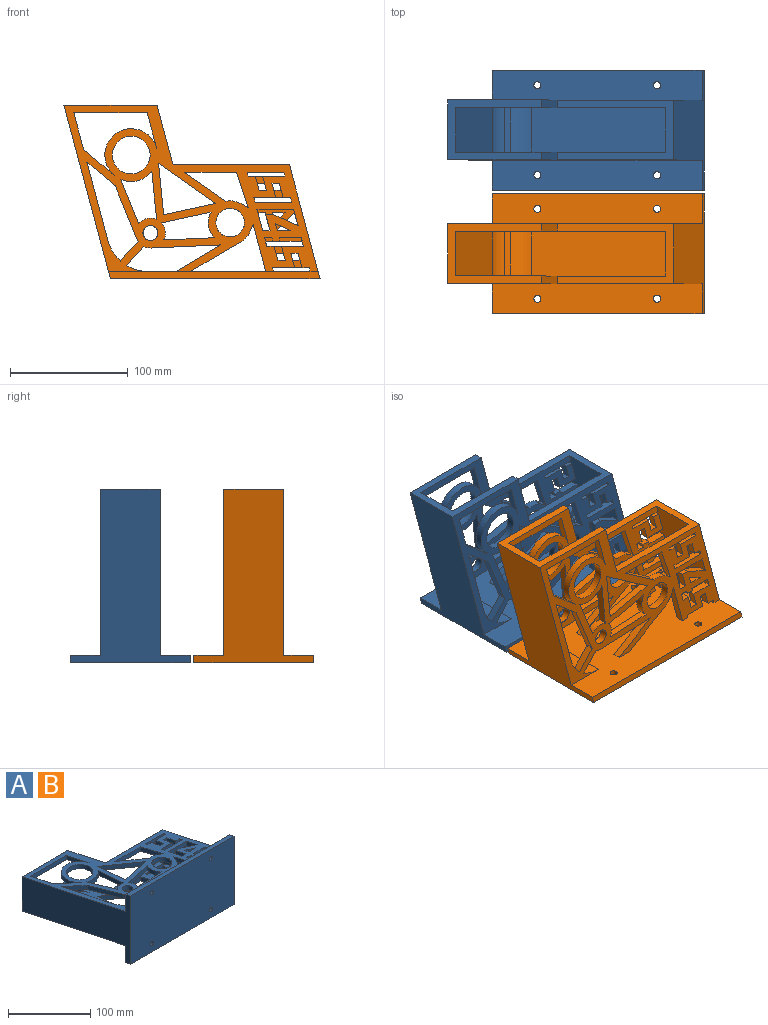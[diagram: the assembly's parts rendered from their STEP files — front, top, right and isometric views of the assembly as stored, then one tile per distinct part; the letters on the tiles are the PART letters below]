
ASSEMBLY  parts=2 mates=1
PART A: 172 faces, bbox 217.1x147.2x101.6 mm
  f0: plane 16.15x14.78mm, normal (0.74,-0.68,0), area 139mm2, adj f15,f17,f53,f170
  f1: plane 177.63x101.6mm, normal (0,1,0), area 15687.5mm2, adj f2,f6,f10,f15,f16,f17,f19,f22
  f2: plane 215.38x140.86mm, normal (0,0,1), area 9095.8mm2, adj f1,f3,f11,f12,f13,f14,f18,f19
  f3: cylinder r=18.51mm len=8.94mm, axis (0,0,1), area 76.2mm2, adj f2,f16,f84,f162
  f4: cylinder r=18.51mm len=13.03mm, axis (0,0,-1), area 85.7mm2, adj f15,f17,f153,f160
  f5: plane 30.14x9.86mm, normal (-0.95,-0.31,0), area 201.3mm2, adj f15,f17,f154,f160
  f6: plane 40.06x10.73mm, normal (-0.97,-0.26,0), area 263.3mm2, adj f1,f15,f17,f159
  f7: plane 7.17x6.35mm, normal (0.97,0.26,0), area 47.1mm2, adj f15,f17,f135,f152
  f8: plane 18.05x6.35mm, normal (0.97,0.26,0), area 118.7mm2, adj f15,f17,f130,f134
  f9: plane 6.35x4.2mm, normal (0.97,0.26,0), area 27.6mm2, adj f15,f17,f125,f129
  f10: plane 6.35x3.18mm, normal (0.97,0.26,0), area 20.9mm2, adj f1,f15,f17,f124
  f11: plane 7.21x6.35mm, normal (0.97,0.26,0), area 47.4mm2, adj f2,f16,f100,f109
  f12: plane 18.01x6.35mm, normal (0.97,0.26,0), area 118.4mm2, adj f2,f16,f96,f99
  f13: plane 6.35x4.2mm, normal (0.97,0.26,0), area 27.6mm2, adj f2,f16,f86,f95
  f14: plane 6.35x3.18mm, normal (0.97,0.26,0), area 20.9mm2, adj f2,f16,f82,f85
  f15: plane 201.38x140.86mm, normal (0,0,1), area 7397.1mm2, adj f0,f1,f4,f5,f6,f7,f8,f9
  f16: plane 201.38x140.86mm, normal (0,0,-1), area 7441.4mm2, adj f1,f3,f11,f12,f13,f14,f18,f20
  f17: plane 215.38x140.86mm, normal (0,0,-1), area 9051.5mm2, adj f0,f1,f4,f5,f6,f7,f8,f9
  f18: plane 115.46x50.8mm, normal (0.97,0.26,0), area 5847.6mm2, adj f2,f15,f16,f17,f20,f33,f34,f55
  f19: plane 101.6x96.58mm, normal (0.97,0.26,0), area 5413.5mm2, adj f1,f2,f17,f23,f25,f163,f164
  f20: plane 78.89x50.8mm, normal (0,1,0), area 1252.3mm2, adj f2,f15,f16,f17,f18,f21,f22,f28
  f21: plane 50.62x13.56mm, normal (0.97,0.26,0), area 332.8mm2, adj f2,f16,f20,f25
  f22: plane 147.21x101.6mm, normal (-0.97,-0.26,0), area 8075.9mm2, adj f1,f2,f17,f20,f23,f163,f164
  f23: plane 177.63x101.6mm, normal (0,-1,0), area 17932.8mm2, adj f19,f22,f163,f164,f165,f166,f167,f168
  f24: cylinder r=16mm len=32mm, axis (0,0,1), area 638.5mm2, adj f2,f16
  f25: plane 98.75x50.8mm, normal (0,1,0), area 1504.5mm2, adj f2,f15,f16,f17,f19,f21,f28,f32
  f26: cylinder r=6.35mm len=12.7mm, axis (0,0,1), area 253.4mm2, adj f2,f16
  f27: cylinder r=12.16mm len=24.32mm, axis (0,0,1), area 485.1mm2, adj f2,f16
  f28: plane 50.62x13.56mm, normal (0.97,0.26,0), area 332.8mm2, adj f15,f17,f20,f25
  f29: cylinder r=6.35mm len=12.7mm, axis (0,0,-1), area 253.4mm2, adj f15,f17
  f30: cylinder r=12.16mm len=24.32mm, axis (0,0,-1), area 485.1mm2, adj f15,f17
  f31: cylinder r=16mm len=32mm, axis (0,0,1), area 638.5mm2, adj f15,f17
  f32: plane 90.23x50.8mm, normal (-0.97,-0.26,0), area 4002.5mm2, adj f1,f2,f15,f16,f17,f25,f62,f82
  f33: plane 26x21.92mm, normal (0.64,0.76,0), area 215.9mm2, adj f15,f17,f18,f36
  f34: plane 62.26x6.35mm, normal (0,-1,0), area 395.3mm2, adj f15,f17,f18,f35
  f35: plane 30.18x8.09mm, normal (-0.97,-0.26,0), area 198.4mm2, adj f15,f17,f34,f36
  f36: cylinder r=22.35mm len=43.94mm, axis (0,0,1), area 532.3mm2, adj f15,f17,f33,f35
  f37: plane 48.53x34.15mm, normal (-0.58,-0.82,0), area 376.8mm2, adj f15,f17,f38,f39
  f38: plane 44.16x9.65mm, normal (-0.21,0.98,0), area 287mm2, adj f15,f17,f37,f39
  f39: plane 43.8x6.35mm, normal (1,0.1,0), area 279.5mm2, adj f15,f17,f37,f38
  f40: plane 40.57x6.35mm, normal (-1,-0.1,0), area 258.9mm2, adj f15,f17,f41,f43
  f41: cylinder r=12.7mm len=15.24mm, axis (0,0,1), area 107.4mm2, adj f15,f17,f40,f42
  f42: plane 37.8x15.27mm, normal (0.93,0.37,0), area 258.9mm2, adj f15,f17,f41,f43
  f43: cylinder r=22.35mm len=26.46mm, axis (0,0,1), area 186.1mm2, adj f15,f17,f40,f42
  f44: cylinder r=18.51mm len=21.66mm, axis (0,0,1), area 148.4mm2, adj f15,f17,f45,f47
  f45: plane 42.89x6.35mm, normal (-0.04,1,0), area 272.6mm2, adj f15,f17,f44,f46
  f46: cylinder r=12.7mm len=14.41mm, axis (0,0,1), area 98.2mm2, adj f15,f17,f45,f47
  f47: plane 41.94x9.16mm, normal (0.21,-0.98,0), area 272.6mm2, adj f15,f17,f44,f46
  f48: plane 16.15x14.78mm, normal (0.74,-0.68,0), area 139mm2, adj f2,f16,f54,f170
  f49: plane 37.73x22.39mm, normal (-0.51,0.86,0), area 278.6mm2, adj f1,f15,f17,f51
  f50: plane 37.73x22.39mm, normal (-0.51,0.86,0), area 278.6mm2, adj f1,f2,f16,f52
  f51: plane 59.01x6.35mm, normal (0.04,-1,0), area 375.1mm2, adj f15,f17,f49,f53
  f52: plane 59.01x6.35mm, normal (0.04,-1,0), area 375.1mm2, adj f2,f16,f50,f54
  f53: cylinder r=12.7mm len=6.35mm, axis (0,0,1), area 41mm2, adj f0,f15,f17,f51
  f54: cylinder r=12.7mm len=6.35mm, axis (0,0,1), area 41mm2, adj f2,f16,f48,f52
  f55: plane 23.98x20.21mm, normal (-0.64,-0.76,0), area 199.1mm2, adj f15,f17,f18,f60
  f56: plane 23.98x20.21mm, normal (-0.64,-0.76,0), area 199.1mm2, adj f2,f16,f18,f61
  f57: plane 50.8x16.52mm, normal (-0.74,0.68,0), area 309.5mm2, adj f2,f15,f16,f17,f58,f59,f169,f171
  f58: cylinder r=12.7mm len=6.35mm, axis (0,0,1), area 17.6mm2, adj f15,f17,f57,f60
  f59: cylinder r=12.7mm len=6.35mm, axis (0,0,1), area 17.6mm2, adj f2,f16,f57,f61
  f60: plane 44.73x18.07mm, normal (-0.93,-0.37,0), area 306.3mm2, adj f15,f17,f55,f58
  f61: plane 44.73x18.07mm, normal (-0.93,-0.37,0), area 306.3mm2, adj f2,f16,f56,f59
  f62: plane 31.13x6.35mm, normal (0,-1,0), area 197.7mm2, adj f15,f17,f32,f63
  f63: plane 6.35x3.18mm, normal (0.97,0.26,0), area 20.9mm2, adj f15,f17,f62,f143
  f64: plane 42.73x25.36mm, normal (0.51,-0.86,0), area 315.5mm2, adj f1,f15,f17,f65
  f65: cylinder r=18.51mm len=8.94mm, axis (0,0,1), area 76.2mm2, adj f15,f17,f64,f159
  f66: cylinder r=22.35mm len=43.94mm, axis (0,0,1), area 532.3mm2, adj f2,f16,f67,f69
  f67: plane 30.18x8.09mm, normal (-0.97,-0.26,0), area 198.4mm2, adj f2,f16,f66,f68
  f68: plane 62.26x6.35mm, normal (0,-1,0), area 395.3mm2, adj f2,f16,f18,f67
  f69: plane 26x21.92mm, normal (0.64,0.76,0), area 215.9mm2, adj f2,f16,f18,f66
  f70: plane 43.8x6.35mm, normal (1,0.1,0), area 279.5mm2, adj f2,f16,f71,f72
  f71: plane 44.16x9.65mm, normal (-0.21,0.98,0), area 287mm2, adj f2,f16,f70,f72
  f72: plane 48.53x34.15mm, normal (-0.58,-0.82,0), area 376.8mm2, adj f2,f16,f70,f71
  f73: cylinder r=22.35mm len=26.46mm, axis (0,0,1), area 186.1mm2, adj f2,f16,f74,f76
  f74: plane 37.8x15.27mm, normal (0.93,0.37,0), area 258.9mm2, adj f2,f16,f73,f75
  f75: cylinder r=12.7mm len=15.24mm, axis (0,0,1), area 107.4mm2, adj f2,f16,f74,f76
  f76: plane 40.57x6.35mm, normal (-1,-0.1,0), area 258.9mm2, adj f2,f16,f73,f75
  f77: plane 41.94x9.16mm, normal (0.21,-0.98,0), area 272.6mm2, adj f2,f16,f78,f80
  f78: cylinder r=12.7mm len=14.41mm, axis (0,0,1), area 98.2mm2, adj f2,f16,f77,f79
  f79: plane 42.89x6.35mm, normal (-0.04,1,0), area 272.6mm2, adj f2,f16,f78,f80
  f80: cylinder r=18.51mm len=21.66mm, axis (0,0,1), area 148.4mm2, adj f2,f16,f77,f79
  f81: plane 6.35x3.18mm, normal (0.97,0.26,0), area 20.9mm2, adj f1,f2,f16,f110
  f82: plane 31.13x6.35mm, normal (0,-1,0), area 197.7mm2, adj f2,f14,f16,f32
  f83: plane 40.06x10.73mm, normal (-0.97,-0.26,0), area 263.3mm2, adj f1,f2,f16,f162
  f84: plane 42.73x25.36mm, normal (0.51,-0.86,0), area 315.5mm2, adj f1,f2,f3,f16
  f85: plane 6.35x6.23mm, normal (0,1,0), area 39.5mm2, adj f2,f14,f16,f94
  f86: plane 18.68x6.35mm, normal (0,-1,0), area 118.6mm2, adj f2,f13,f16,f87
  f87: plane 12.03x6.35mm, normal (0.97,0.26,0), area 79.1mm2, adj f2,f16,f86,f88
  f88: plane 6.35x6.23mm, normal (0,-1,0), area 39.5mm2, adj f2,f16,f87,f89
  f89: plane 12.03x6.35mm, normal (-0.97,-0.26,0), area 79.1mm2, adj f2,f16,f88,f90
  f90: plane 6.35x6.23mm, normal (0,-1,0), area 39.5mm2, adj f2,f16,f32,f89
  f91: plane 18.68x6.35mm, normal (0,1,0), area 118.6mm2, adj f2,f16,f32,f92
  f92: plane 12.03x6.35mm, normal (-0.97,-0.26,0), area 79.1mm2, adj f2,f16,f91,f93
  f93: plane 6.35x6.23mm, normal (0,1,0), area 39.5mm2, adj f2,f16,f92,f94
  f94: plane 12.03x6.35mm, normal (0.97,0.26,0), area 79.1mm2, adj f2,f16,f85,f93
  f95: plane 31.13x6.35mm, normal (0,1,0), area 197.7mm2, adj f2,f13,f16,f32
  f96: plane 31.13x6.35mm, normal (0,-1,0), area 197.7mm2, adj f2,f12,f16,f32
  f97: plane 11.57x6.35mm, normal (0,1,0), area 73.4mm2, adj f2,f16,f98,f108
  f98: plane 6.35x6.01mm, normal (0.97,0.26,0), area 39.5mm2, adj f2,f16,f97,f108
  f99: plane 6.35x6.23mm, normal (0,1,0), area 39.5mm2, adj f2,f12,f16,f107
  f100: plane 6.35x6.23mm, normal (0,-1,0), area 39.5mm2, adj f2,f11,f16,f101
  f101: plane 6.35x3.01mm, normal (-0.97,-0.26,0), area 19.8mm2, adj f2,f16,f100,f102
  f102: plane 6.35x6.23mm, normal (0,-1,0), area 39.5mm2, adj f2,f16,f101,f103
  f103: plane 6.35x3.01mm, normal (0.97,0.26,0), area 19.8mm2, adj f2,f16,f102,f104
  f104: plane 18.68x6.35mm, normal (0,-1,0), area 118.6mm2, adj f2,f16,f32,f103
  f105: plane 21.28x9.71mm, normal (0.42,0.91,0), area 148.5mm2, adj f2,f16,f32,f106
  f106: plane 6.35x6.23mm, normal (0,1,0), area 39.5mm2, adj f2,f16,f105,f107
  f107: plane 13.81x6.35mm, normal (-0.97,-0.26,0), area 90.8mm2, adj f2,f16,f99,f106
  f108: plane 13.18x6.35mm, normal (-0.42,-0.91,0), area 92mm2, adj f2,f16,f97,f98
  f109: plane 6.35x6.23mm, normal (0,1,0), area 39.5mm2, adj f2,f11,f16,f118
  f110: plane 18.68x6.35mm, normal (0,-1,0), area 118.6mm2, adj f2,f16,f81,f111
  f111: plane 12.03x6.35mm, normal (0.97,0.26,0), area 79.1mm2, adj f2,f16,f110,f112
  f112: plane 6.35x6.23mm, normal (0,-1,0), area 39.5mm2, adj f2,f16,f111,f113
  f113: plane 12.03x6.35mm, normal (-0.97,-0.26,0), area 79.1mm2, adj f2,f16,f112,f114
  f114: plane 6.35x6.23mm, normal (0,-1,0), area 39.5mm2, adj f2,f16,f32,f113
  f115: plane 18.68x6.35mm, normal (0,1,0), area 118.6mm2, adj f2,f16,f32,f116
  f116: plane 12.03x6.35mm, normal (-0.97,-0.26,0), area 79.1mm2, adj f2,f16,f115,f117
  f117: plane 6.35x6.23mm, normal (0,1,0), area 39.5mm2, adj f2,f16,f116,f118
  f118: plane 12.03x6.35mm, normal (0.97,0.26,0), area 79.1mm2, adj f2,f16,f109,f117
  f119: plane 6.35x6.23mm, normal (0,1,0), area 39.5mm2, adj f15,f17,f32,f128
  f120: plane 18.68x6.35mm, normal (0,-1,0), area 118.6mm2, adj f15,f17,f32,f121
  f121: plane 12.03x6.35mm, normal (-0.97,-0.26,0), area 79.1mm2, adj f15,f17,f120,f122
  f122: plane 6.35x6.23mm, normal (0,-1,0), area 39.5mm2, adj f15,f17,f121,f123
  f123: plane 12.03x6.35mm, normal (0.97,0.26,0), area 79.1mm2, adj f15,f17,f122,f124
  f124: plane 6.35x6.23mm, normal (0,-1,0), area 39.5mm2, adj f10,f15,f17,f123
  f125: plane 18.68x6.35mm, normal (0,1,0), area 118.6mm2, adj f9,f15,f17,f126
  f126: plane 12.03x6.35mm, normal (0.97,0.26,0), area 79.1mm2, adj f15,f17,f125,f127
  f127: plane 6.35x6.23mm, normal (0,1,0), area 39.5mm2, adj f15,f17,f126,f128
  f128: plane 12.03x6.35mm, normal (-0.97,-0.26,0), area 79.1mm2, adj f15,f17,f119,f127
  f129: plane 31.13x6.35mm, normal (0,-1,0), area 197.7mm2, adj f9,f15,f17,f32
  f130: plane 31.13x6.35mm, normal (0,1,0), area 197.7mm2, adj f8,f15,f17,f32
  f131: plane 14.97x13.85mm, normal (0.68,-0.73,0), area 129.5mm2, adj f15,f17,f32,f132
  f132: plane 6.35x6.23mm, normal (0,-1,0), area 39.5mm2, adj f15,f17,f131,f133
  f133: plane 13.85x6.35mm, normal (-0.97,-0.26,0), area 91mm2, adj f15,f17,f132,f134
  f134: plane 6.35x6.23mm, normal (0,-1,0), area 39.5mm2, adj f8,f15,f17,f133
  f135: plane 6.35x6.23mm, normal (0,1,0), area 39.5mm2, adj f7,f15,f17,f136
  f136: plane 6.35x3.01mm, normal (-0.97,-0.26,0), area 19.8mm2, adj f15,f17,f135,f137
  f137: plane 6.35x6.23mm, normal (0,1,0), area 39.5mm2, adj f15,f17,f136,f138
  f138: plane 6.35x3.01mm, normal (0.97,0.26,0), area 19.8mm2, adj f15,f17,f137,f142
  f139: plane 10.57x6.35mm, normal (0,-1,0), area 67.1mm2, adj f15,f17,f140,f141
  f140: plane 7.83x6.35mm, normal (0.97,0.26,0), area 51.5mm2, adj f15,f17,f139,f141
  f141: plane 8.47x7.83mm, normal (-0.68,0.73,0), area 73.3mm2, adj f15,f17,f139,f140
  f142: plane 18.68x6.35mm, normal (0,1,0), area 118.6mm2, adj f15,f17,f32,f138
  f143: plane 18.68x6.35mm, normal (0,1,0), area 118.6mm2, adj f15,f17,f63,f144
  f144: plane 12.03x6.35mm, normal (0.97,0.26,0), area 79.1mm2, adj f15,f17,f143,f145
  f145: plane 6.35x6.23mm, normal (0,1,0), area 39.5mm2, adj f15,f17,f144,f146
  f146: plane 12.03x6.35mm, normal (-0.97,-0.26,0), area 79.1mm2, adj f15,f17,f145,f147
  f147: plane 6.35x6.23mm, normal (0,1,0), area 39.5mm2, adj f15,f17,f32,f146
  f148: plane 18.68x6.35mm, normal (0,-1,0), area 118.6mm2, adj f15,f17,f32,f149
  f149: plane 12.03x6.35mm, normal (-0.97,-0.26,0), area 79.1mm2, adj f15,f17,f148,f150
  f150: plane 6.35x6.23mm, normal (0,-1,0), area 39.5mm2, adj f15,f17,f149,f151
  f151: plane 12.03x6.35mm, normal (0.97,0.26,0), area 79.1mm2, adj f15,f17,f150,f152
  f152: plane 6.35x6.23mm, normal (0,-1,0), area 39.5mm2, adj f7,f15,f17,f151
  f153: plane 34.79x24.49mm, normal (0.58,0.82,0), area 270.2mm2, adj f4,f15,f17,f154
  f154: plane 44.08x6.35mm, normal (0,-1,0), area 279.9mm2, adj f5,f15,f17,f153
  f155: plane 44.08x6.35mm, normal (0,-1,0), area 279.9mm2, adj f2,f16,f156,f158
  f156: plane 30.14x9.86mm, normal (-0.95,-0.31,0), area 201.3mm2, adj f2,f16,f155,f161
  f157: cylinder r=18.51mm len=13.03mm, axis (0,0,-1), area 85.7mm2, adj f2,f16,f158,f161
  f158: plane 34.79x24.49mm, normal (0.58,0.82,0), area 270.2mm2, adj f2,f16,f155,f157
  f159: plane 6.35x5.76mm, normal (0.93,-0.38,0), area 39.5mm2, adj f6,f15,f17,f65
  f160: plane 6.35x6.11mm, normal (0.5,0.87,0), area 44.9mm2, adj f4,f5,f15,f17
  f161: plane 6.35x6.11mm, normal (0.5,0.87,0), area 44.9mm2, adj f2,f16,f156,f157
  f162: plane 6.35x5.76mm, normal (0.93,-0.38,0), area 39.5mm2, adj f2,f3,f16,f83
  f163: plane 179.34x6.35mm, normal (0,0,1), area 1128mm2, adj f1,f19,f22,f23
  f164: plane 179.34x6.35mm, normal (0,0,-1), area 1128mm2, adj f1,f19,f22,f23
  f165: cylinder r=3.02mm len=6.35mm, axis (0,1,0), area 120.6mm2, adj f1,f23
  f166: cylinder r=3.02mm len=6.35mm, axis (0,1,0), area 120.6mm2, adj f1,f23
  f167: cylinder r=3.02mm len=6.35mm, axis (0,1,0), area 120.6mm2, adj f1,f23
  f168: cylinder r=3.02mm len=6.35mm, axis (0,1,0), area 120.6mm2, adj f1,f23
  f169: cylinder r=34.27mm len=50.8mm, axis (0,0,1), area 1006.4mm2, adj f2,f17,f18,f57
  f170: cylinder r=34.27mm len=50.8mm, axis (0,0,1), area 947.7mm2, adj f0,f1,f2,f17,f48,f171
  f171: plane 38.1x4.69mm, normal (0.68,0.74,0), area 241.9mm2, adj f15,f16,f57,f170
PART B: same geometry as A
PLACE A rot(axis=(1,0,0),90deg) t=(-29.39,174.48,79.03)mm
PLACE B rot(axis=(1,0,0),90deg) t=(-29.39,69.71,79.03)mm
MATE fastened A.f1 <-> B.f1  axis (0,0,1) through (11.84,142.73,9.96)mm
